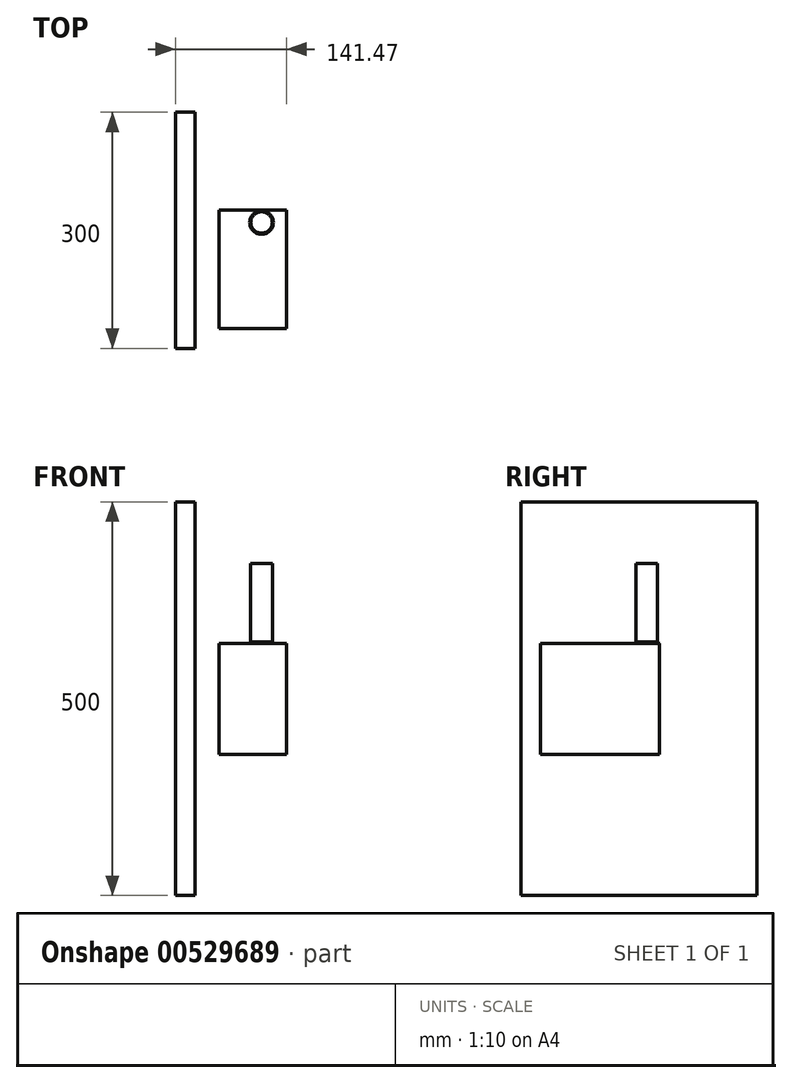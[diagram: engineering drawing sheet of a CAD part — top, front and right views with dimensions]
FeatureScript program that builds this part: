
annotation { "Feature Type Name" : "Feature", "Feature Type Description" : "" }
export const myFeature = defineFeature(function(context is Context, id is Id, definition is map)
    precondition{}
    {
        {
            var Q0;
            Q0=qCreatedBy(makeId("Right.planeOp"),FACE);
            var sketch = newSketch(context, id + "F0", { "sketchPlane" : qUnion([Q0])});
            skLineSegment(sketch, "E0.bottom", {"start": v(88.65, 69.94) * mm, "end": v(-62.35, 69.94) * mm});
            skLineSegment(sketch, "E0.top", {"start": v(88.65, -71.06) * mm, "end": v(-62.35, -71.06) * mm});
            skLineSegment(sketch, "E0.left", {"start": v(88.65, 69.94) * mm, "end": v(88.65, -71.06) * mm});
            skLineSegment(sketch, "E0.right", {"start": v(-62.35, 69.94) * mm, "end": v(-62.35, -71.06) * mm});
            skSolve(sketch);
        }
        {
            var Q0;
            Q0=qSketchRegion(id+"F0",true);
            extrude(context, id + "F1", {"entities" : qUnion([Q0]), "depth" : 86 * mm});
        }
        {
            var Q0;
            Q0=makeQuery(id+"F1.opExtrude","SWEPT_FACE",FACE,{"disambiguationData":[OSD([sQuery(id+"F0.wireOp",EDGE,"E0.bottom")])]});
            var sketch = newSketch(context, id + "F2", { "sketchPlane" : qUnion([Q0])});
            skCircle(sketch, "E1", {"center": v(54, 72.65) * mm, "radius": 15 * mm});
            skSolve(sketch);
        }
        {
            var Q0;
            Q0=qSketchRegion(id+"F2",true);
            extrude(context, id + "F3", {"entities" : qUnion([Q0]), "operationType" : NewBodyOperationType.ADD, "depth" : 2 * mm});
        }
        {
            var Q0;
            Q0=makeQuery(id+"F3.opExtrude","CAP_FACE",FACE,{"disambiguationData":[OSD([sQuery(id+"F2.wireOp",EDGE,"E1")])],"isStart":false});
            var sketch = newSketch(context, id + "F4", { "sketchPlane" : qUnion([Q0])});
            skCircle(sketch, "E2", {"center": v(54, 72.65) * mm, "radius": 13.69 * mm});
            skSolve(sketch);
        }
        {
            var Q0;
            Q0=qSketchRegion(id+"F4",true);
            extrude(context, id + "F5", {"entities" : qUnion([Q0]), "operationType" : NewBodyOperationType.ADD, "depth" : 100 * mm});
        }
        {
            var Q0;
            Q0=qCreatedBy(makeId("Top.planeOp"),FACE);
            var sketch = newSketch(context, id + "F6", { "sketchPlane" : qUnion([Q0])});
            skLineSegment(sketch, "E3.bottom", {"start": v(-55.47, 212.78) * mm, "end": v(-30.47, 212.78) * mm});
            skLineSegment(sketch, "E3.top", {"start": v(-55.47, -87.22) * mm, "end": v(-30.47, -87.22) * mm});
            skLineSegment(sketch, "E3.left", {"start": v(-55.47, 212.78) * mm, "end": v(-55.47, -87.22) * mm});
            skLineSegment(sketch, "E3.right", {"start": v(-30.47, 212.78) * mm, "end": v(-30.47, -87.22) * mm});
            skSolve(sketch);
        }
        {
            var Q0;
            Q0=makeQuery(id+"F6.imprint","IMPRINT",FACE,{"disambiguationData":[TD([[makeQuery(id+"F6.imprint","IMPRINT",EDGE,{"derivedFrom":sQuery(id+"F6.wireOp",EDGE,"E3.bottom")}),-1.0]])]});
            extrude(context, id + "F7", {"entities" : qUnion([Q0]), "endBound" : BoundingType.SYMMETRIC, "depth" : 500 * mm});
        }
    });
